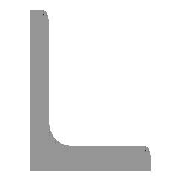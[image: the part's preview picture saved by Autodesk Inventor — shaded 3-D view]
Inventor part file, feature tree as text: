
AUTODESK INVENTOR PART (.ipt)
format: ipt  version: 2024.1 (Build 281209000, 209)  size: 120,832 bytes
history: native  units: mm (DEFAULTED — no unit token found)
features: other x4, sketch x1, plane x1
ambient origin geometry x8: Origin, YZ Plane, XZ Plane, XY Plane, X Axis, Y Axis, Z Axis, Center Point
bodies: Solid1 (feature_tree), Body (feature_tree)
feature tree (6):
  parser-record x1  (decoder bookkeeping rows leaked as tree rows — omitted from the tree; the rows remain in map.json)
  other  "Driven Length"
  other  "Start Plane"
  other  "End Plane"
  sketch  "Sketch3"  dims[d0=28.702mm d1=28.702mm d2=3.175mm d3=3.175mm d4=860.0mm d5=0.0mm d10=0.0mm d11=0.0mm d12=-0.0mm d13=860.0mm d14=2.286mm d15=1.27mm d16=90.0deg d17=860.0mm]
  plane  "Work Plane3"
